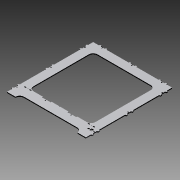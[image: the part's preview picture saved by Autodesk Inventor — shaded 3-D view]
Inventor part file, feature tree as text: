
AUTODESK INVENTOR PART (.ipt)
format: ipt  version: 2013 (Build 170138000, 138)  size: 791,552 bytes
history: native  units: mm
features: extrude x8, sketch x8, other x3, fillet x3, reference x2
ambient origin geometry x8: Origin, YZ Plane, XZ Plane, XY Plane, X Axis, Y Axis, Z Axis, Center Point
bodies: Solid1 (feature_tree)
feature tree (24):
  other  "BACK PLATE.ipt"
  extrude  "Extrusion1"  Depth=10.0mm TaperAngle=0.0deg
  fillet  "Fillet1"  Radius=25.0mm
  extrude  "Extrusion2"  Depth=10.0mm TaperAngle=0.0deg
  extrude  "Extrusion3"  Depth=10.0mm TaperAngle=0.0deg
  extrude  "Extrusion4"  Depth=10.0mm TaperAngle=0.0deg
  extrude  "Extrusion5"  Depth=31.3mm
  fillet  "Fillet2"  Radius=27.3mm
  extrude  "Extrusion6"  Depth=3.0mm
  fillet  "Fillet3"  Radius=25.0mm
  extrude  "Extrusion7"  Depth=2.5mm
  extrude  "Extrusion8"  Depth=10.0mm
  other  "Solid1::BACK PLATE.ipt"
  other  "TaggingFeature1"
  sketch  "Sketch1"  dims[d0=10.0mm d1=10.0mm d2=0.0mm d3=25.0mm]
  sketch  "Sketch2"  dims[d4=40.0mm d5=10.0mm d6=0.0mm]
  sketch  "Sketch4"  dims[d7=25.0mm d9=10.0mm d10=0.0mm]
  sketch  "Sketch5"  dims[d11=10.0mm d12=0.0mm d13=10.0mm d14=0.0mm]
  sketch  "Sketch6"  dims[d15=2.0mm d16=31.3mm d18=27.3mm]
  reference  "Reference1"
  reference  "Reference2"
  sketch  "Sketch7"  dims[d19=36.0mm d20=3.0mm d21=25.0mm]
  sketch  "Sketch8"  dims[d22=10.0mm d23=0.0mm d24=2.5mm]
  sketch  "Sketch9"  dims[d25=1.5mm d27=10.0mm d28=10.0mm d29=0.0mm d30=10.0mm d31=0.0mm]
